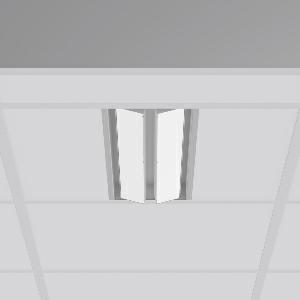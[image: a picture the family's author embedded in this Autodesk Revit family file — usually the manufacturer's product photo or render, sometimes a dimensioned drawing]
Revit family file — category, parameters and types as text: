
# Revit family: tx-move_901735_004_1_5421
name_source: partatom
category: Lighting Fixtures
units: mm (PartAtom-declared; Revit-internal decimal feet)

## family parameters
Cut with Voids When Loaded = No
Host = Face
Light Source = No
Part Type = Normal
Room Calculation Point = No
Round Connector Dimension = Use Diameter
Shared = No

## types (1)
- MultiLumen 1 (1 x LED Modul 840, 2450 lm, 4000)
    Apparent Load = 35 VA
    Approval mark = CE
    CIE Flux Codes = 47 79 96 100 100
    Color Rendering = 80
    Color Temperature = 4000
    Default Elevation = 1800 mm
    Description = Series: TX-MOVE
Einlege/Einbau-Flächenstrahler. Housing: sheet steel, powder-coated. 2xSwivel range: 90°. High-efficiency LED units with flush-mounted opal diffuser made of non-yellowing PMMA. Symmetrical wide beam light emission. Suitable for laying in grid ceiling module 600. Connected converter included in separate gearbox.Suitable for through-wiring.MultiLumen: Luminous flux adjustable in 3 steps. Accessories: Mounting frame for installation in suspended ceilings. Environmentally friendly and resource-saving due to replaceable and recyclable components. 
Colour: silver, matt (approx. RAL 9006)
Length: 597 mm
Width: 190 mm
Height: 39 mm
Cut-out length: 577.5 mm
Cut-out width: 174 mm
Recess height: 100 mm
Lamp: LED
Socket: without socket
Colour temperature: 4000K
Colour rendering index (CRI): 80
System power: 35 W
Rated luminous flux: 4900 lm
Luminous efficiency: 140 lm/W
System power 2: 47 W
Rated luminous flux 2: 6450 lm
Luminous efficiency 2: 137 lm/W
System power 3: 68 W
Rated luminous flux 3: 8750 lm
Luminous efficiency 3: 129 lm/W
Control gear: Regulated power supply
Protection class: I
Type of protection: IP 20
    Height = 0 mm  [stored 0 ft]
    Lamp = 1 x LED Modul 840
    Lamp Light Flux = 2450 lm
    Lamp count = 1
    Length = 597 mm
    Lifetime = 50000 h
    Luminous efficacy = 140 lm/W
    Manufacturer = RZB
    ModVariant = No
    Model = 901735.004.1
    Mounting Place = Ceiling, Wall
    Mounting Type = Recessed
    Number of Poles = 1
    OnlyDefault = Yes
    Power Factor = 1
    Product Name = TX-MOVE
    Product group = Recessed projectors
    ProductGroupID = 401
    Protection Class = Protection class I
    Protection Degree = IP 20
    RLX_Detail_Level = 1
    RLX_Emergency_Light_Flux = 0 lm
    RLX_Emergency_Type = 0
    RLX_Emergency_Type_DB = No
    RlxData = <blob elided: 30969 chars, md5=0996174d>
    Socket = socket
    Standby Power = 0 W
    System Light Flux = 4900 lm
    System Power = 35 W
    Type Comments = MultiLumen 1
    Type Image = 901735.004.jpg
    URL = http://relux.com
    VarID = multilumen_1
    Voltage = 230 V
    Voltage Range = 220-240 V
    Weight = 0.00 kg
    Width = 190 mm  [stored 0.62336 ft]

note: [stored X ft] marks values corroborated as IEEE doubles in the binary element streams (Revit-internal decimal feet)

## geometry (parser evidence)
native form markers: Blend x4, Sweep x14
no freeform markers — native parametric forms only
